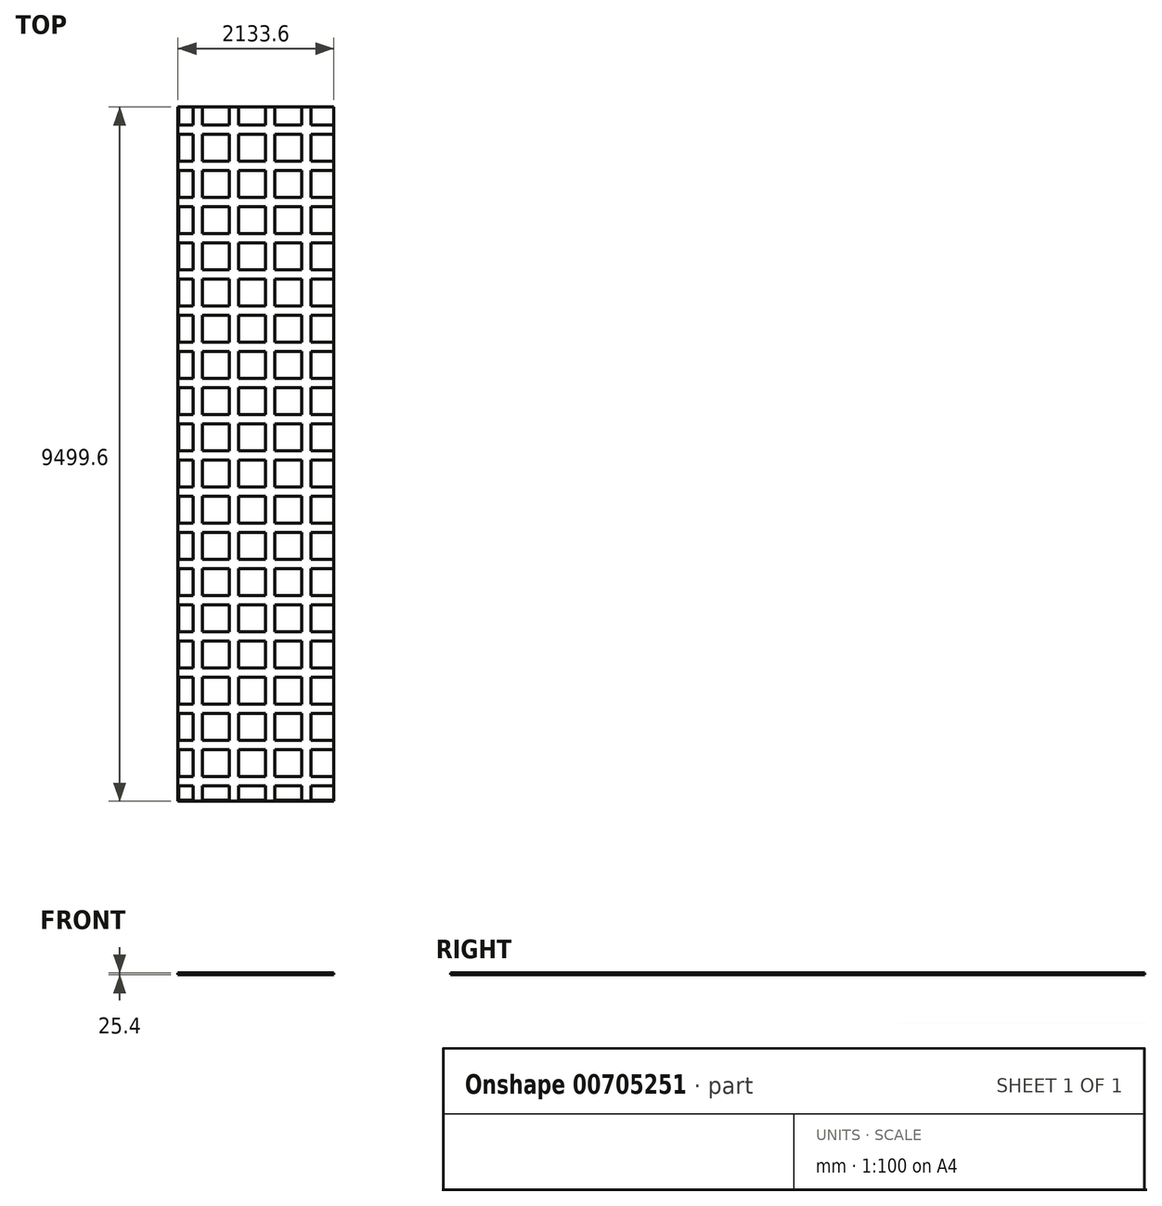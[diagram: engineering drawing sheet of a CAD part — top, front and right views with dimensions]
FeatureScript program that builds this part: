
annotation { "Feature Type Name" : "Feature", "Feature Type Description" : "" }
export const myFeature = defineFeature(function(context is Context, id is Id, definition is map)
    precondition{}
    {
        {
            var Q0;
            Q0=qCreatedBy(makeId("Top.planeOp"),FACE);
            var sketch = newSketch(context, id + "F0", { "sketchPlane" : qUnion([Q0])});
            skLineSegment(sketch, "E0.bottom", {"start": v(0, 0) * mm, "end": v(2133.6, 0) * mm});
            skLineSegment(sketch, "E0.top", {"start": v(0, 9499.6) * mm, "end": v(2133.6, 9499.6) * mm});
            skLineSegment(sketch, "E0.left", {"start": v(0, 0) * mm, "end": v(0, 9499.6) * mm});
            skLineSegment(sketch, "E0.right", {"start": v(2133.6, 0) * mm, "end": v(2133.6, 9499.6) * mm});
            skSolve(sketch);
        }
        {
            var Q0;
            Q0=makeQuery(id+"F0.imprint","IMPRINT",FACE,{"disambiguationData":[TD([[makeQuery(id+"F0.imprint","IMPRINT",EDGE,{"derivedFrom":sQuery(id+"F0.wireOp",EDGE,"E0.bottom")}),1.0]])]});
            extrude(context, id + "F1", {"entities" : qUnion([Q0]), "depth" : 25.4 * mm, "offsetDistance" : 25.4 * mm});
        }
        {
            var Q0;
            Q0=makeQuery(id+"F1.opExtrude","CAP_FACE",FACE,{"disambiguationData":[OSD([sQuery(id+"F0.wireOp",EDGE,"E0.bottom"),sQuery(id+"F0.wireOp",EDGE,"E0.top"),sQuery(id+"F0.wireOp",EDGE,"E0.left"),sQuery(id+"F0.wireOp",EDGE,"E0.right")])],"isStart":false});
            var sketch = newSketch(context, id + "F2", { "sketchPlane" : qUnion([Q0])});
            skLineSegment(sketch, "E1.0", {"start": v(12.7, 0) * mm, "end": v(12.7, 9499.6) * mm});
            skLineSegment(sketch, "E2", {"start": v(336.55, 12.7) * mm, "end": v(336.55, 9499.6) * mm});
            skLineSegment(sketch, "E3.0", {"start": v(0, 12.7) * mm, "end": v(2133.6, 12.7) * mm});
            skLineSegment(sketch, "E4", {"start": v(12.7, 336.55) * mm, "end": v(2133.6, 336.55) * mm});
            skLineSegment(sketch, "E5.0", {"start": v(209.55, 12.7) * mm, "end": v(209.55, 9499.6) * mm});
            skLineSegment(sketch, "E6.0", {"start": v(12.7, 209.55) * mm, "end": v(2133.6, 209.55) * mm});
            skLineSegment(sketch, "E7.1.0.0", {"start": v(704.85, 12.7) * mm, "end": v(704.85, 9499.6) * mm});
            skLineSegment(sketch, "E7.1.0.1", {"start": v(831.85, 12.7) * mm, "end": v(831.85, 9499.6) * mm});
            skLineSegment(sketch, "E7.2.0.0", {"start": v(1200.15, 12.7) * mm, "end": v(1200.15, 9499.6) * mm});
            skLineSegment(sketch, "E7.2.0.1", {"start": v(1327.15, 12.7) * mm, "end": v(1327.15, 9499.6) * mm});
            skLineSegment(sketch, "E7.3.0.0", {"start": v(1695.45, 12.7) * mm, "end": v(1695.45, 9499.6) * mm});
            skLineSegment(sketch, "E7.3.0.1", {"start": v(1822.45, 12.7) * mm, "end": v(1822.45, 9499.6) * mm});
            skLineSegment(sketch, "E7.direction1", {"start": v(209.55, 12.7) * mm, "end": v(704.85, 12.7) * mm, "construction": true});
            skLineSegment(sketch, "E8.0.1.0", {"start": v(12.7, 831.85) * mm, "end": v(2133.6, 831.85) * mm});
            skLineSegment(sketch, "E8.0.1.1", {"start": v(12.7, 704.85) * mm, "end": v(2133.6, 704.85) * mm});
            skLineSegment(sketch, "E8.0.2.0", {"start": v(12.7, 1327.15) * mm, "end": v(2133.6, 1327.15) * mm});
            skLineSegment(sketch, "E8.0.2.1", {"start": v(12.7, 1200.15) * mm, "end": v(2133.6, 1200.15) * mm});
            skLineSegment(sketch, "E8.0.3.0", {"start": v(12.7, 1822.45) * mm, "end": v(2133.6, 1822.45) * mm});
            skLineSegment(sketch, "E8.0.3.1", {"start": v(12.7, 1695.45) * mm, "end": v(2133.6, 1695.45) * mm});
            skLineSegment(sketch, "E8.0.4.0", {"start": v(12.7, 2317.75) * mm, "end": v(2133.6, 2317.75) * mm});
            skLineSegment(sketch, "E8.0.4.1", {"start": v(12.7, 2190.75) * mm, "end": v(2133.6, 2190.75) * mm});
            skLineSegment(sketch, "E8.0.5.0", {"start": v(12.7, 2813.05) * mm, "end": v(2133.6, 2813.05) * mm});
            skLineSegment(sketch, "E8.0.5.1", {"start": v(12.7, 2686.05) * mm, "end": v(2133.6, 2686.05) * mm});
            skLineSegment(sketch, "E8.0.6.0", {"start": v(12.7, 3308.35) * mm, "end": v(2133.6, 3308.35) * mm});
            skLineSegment(sketch, "E8.0.6.1", {"start": v(12.7, 3181.35) * mm, "end": v(2133.6, 3181.35) * mm});
            skLineSegment(sketch, "E8.0.7.0", {"start": v(12.7, 3803.65) * mm, "end": v(2133.6, 3803.65) * mm});
            skLineSegment(sketch, "E8.0.7.1", {"start": v(12.7, 3676.65) * mm, "end": v(2133.6, 3676.65) * mm});
            skLineSegment(sketch, "E8.0.8.0", {"start": v(12.7, 4298.95) * mm, "end": v(2133.6, 4298.95) * mm});
            skLineSegment(sketch, "E8.0.8.1", {"start": v(12.7, 4171.95) * mm, "end": v(2133.6, 4171.95) * mm});
            skLineSegment(sketch, "E8.0.9.0", {"start": v(12.7, 4794.25) * mm, "end": v(2133.6, 4794.25) * mm});
            skLineSegment(sketch, "E8.0.9.1", {"start": v(12.7, 4667.25) * mm, "end": v(2133.6, 4667.25) * mm});
            skLineSegment(sketch, "E8.0.10.0", {"start": v(12.7, 5289.55) * mm, "end": v(2133.6, 5289.55) * mm});
            skLineSegment(sketch, "E8.0.10.1", {"start": v(12.7, 5162.55) * mm, "end": v(2133.6, 5162.55) * mm});
            skLineSegment(sketch, "E8.0.11.0", {"start": v(12.7, 5784.85) * mm, "end": v(2133.6, 5784.85) * mm});
            skLineSegment(sketch, "E8.0.11.1", {"start": v(12.7, 5657.85) * mm, "end": v(2133.6, 5657.85) * mm});
            skLineSegment(sketch, "E8.0.12.0", {"start": v(12.7, 6280.15) * mm, "end": v(2133.6, 6280.15) * mm});
            skLineSegment(sketch, "E8.0.12.1", {"start": v(12.7, 6153.15) * mm, "end": v(2133.6, 6153.15) * mm});
            skLineSegment(sketch, "E8.0.13.0", {"start": v(12.7, 6775.45) * mm, "end": v(2133.6, 6775.45) * mm});
            skLineSegment(sketch, "E8.0.13.1", {"start": v(12.7, 6648.45) * mm, "end": v(2133.6, 6648.45) * mm});
            skLineSegment(sketch, "E8.0.14.0", {"start": v(12.7, 7270.75) * mm, "end": v(2133.6, 7270.75) * mm});
            skLineSegment(sketch, "E8.0.14.1", {"start": v(12.7, 7143.75) * mm, "end": v(2133.6, 7143.75) * mm});
            skLineSegment(sketch, "E8.0.15.0", {"start": v(12.7, 7766.05) * mm, "end": v(2133.6, 7766.05) * mm});
            skLineSegment(sketch, "E8.0.15.1", {"start": v(12.7, 7639.05) * mm, "end": v(2133.6, 7639.05) * mm});
            skLineSegment(sketch, "E8.0.16.0", {"start": v(12.7, 8261.35) * mm, "end": v(2133.6, 8261.35) * mm});
            skLineSegment(sketch, "E8.0.16.1", {"start": v(12.7, 8134.35) * mm, "end": v(2133.6, 8134.35) * mm});
            skLineSegment(sketch, "E8.0.17.0", {"start": v(12.7, 8756.65) * mm, "end": v(2133.6, 8756.65) * mm});
            skLineSegment(sketch, "E8.0.17.1", {"start": v(12.7, 8629.65) * mm, "end": v(2133.6, 8629.65) * mm});
            skLineSegment(sketch, "E8.direction1", {"start": v(12.7, 336.55) * mm, "end": v(38.1, 336.55) * mm, "construction": true});
            skLineSegment(sketch, "E8.direction2", {"start": v(12.7, 336.55) * mm, "end": v(12.7, 831.85) * mm, "construction": true});
            skLineSegment(sketch, "E9.0.0.18", {"start": v(12.7, 9251.95) * mm, "end": v(2133.6, 9251.95) * mm});
            skLineSegment(sketch, "E9.3.0.18", {"start": v(12.7, 9124.95) * mm, "end": v(2133.6, 9124.95) * mm});
            skSolve(sketch);
        }
        {
            var Q0;
            {var subQ0=sQuery(id+"F2.wireOp",EDGE,"E4");var subQ1=sQuery(id+"F2.wireOp",EDGE,"E1.0");var subQ2=makeQuery(id+"F2.imprint","INTERSECT",VERTEX,{"derivedFrom":[subQ1,subQ0]});Q0=makeQuery(id+"F2.imprint","IMPRINT",FACE,{"disambiguationData":[TD([[makeQuery(id+"F2.imprint","IMPRINT",EDGE,{"disambiguationData":[TD([[subQ2,-1.0]])],"derivedFrom":subQ1}),-1.0]])]});}
            var Q1;
            {var subQ0=sQuery(id+"F2.wireOp",EDGE,"E4");var subQ1=sQuery(id+"F2.wireOp",EDGE,"E2");var subQ2=makeQuery(id+"F2.imprint","INTERSECT",VERTEX,{"derivedFrom":[subQ1,subQ0]});Q1=makeQuery(id+"F2.imprint","IMPRINT",FACE,{"disambiguationData":[TD([[makeQuery(id+"F2.imprint","IMPRINT",EDGE,{"disambiguationData":[TD([[subQ2,-1.0]])],"derivedFrom":subQ1}),-1.0]])]});}
            var Q2;
            {var subQ0=sQuery(id+"F2.wireOp",EDGE,"E7.1.0.1");var subQ1=sQuery(id+"F2.wireOp",EDGE,"E4");var subQ2=makeQuery(id+"F2.imprint","INTERSECT",VERTEX,{"derivedFrom":[subQ1,subQ0]});Q2=makeQuery(id+"F2.imprint","IMPRINT",FACE,{"disambiguationData":[TD([[makeQuery(id+"F2.imprint","IMPRINT",EDGE,{"disambiguationData":[TD([[subQ2,-1.0]])],"derivedFrom":subQ1}),1.0]])]});}
            var Q3;
            {var subQ0=sQuery(id+"F2.wireOp",EDGE,"E7.2.0.1");var subQ1=sQuery(id+"F2.wireOp",EDGE,"E4");var subQ2=makeQuery(id+"F2.imprint","INTERSECT",VERTEX,{"derivedFrom":[subQ1,subQ0]});Q3=makeQuery(id+"F2.imprint","IMPRINT",FACE,{"disambiguationData":[TD([[makeQuery(id+"F2.imprint","IMPRINT",EDGE,{"disambiguationData":[TD([[subQ2,-1.0]])],"derivedFrom":subQ1}),1.0]])]});}
            var Q4;
            {var subQ0=sQuery(id+"F2.wireOp",EDGE,"E4");var subQ1=makeQuery(id+"F1.opExtrude","CAP_EDGE",EDGE,{"disambiguationData":[OSD([sQuery(id+"F0.wireOp",EDGE,"E0.right")])],"isStart":false});var subQ2=makeQuery(id+"F2.imprint","INTERSECT",VERTEX,{"derivedFrom":[subQ1,subQ0]});Q4=makeQuery(id+"F2.imprint","IMPRINT",FACE,{"disambiguationData":[TD([[makeQuery(id+"F2.imprint","IMPRINT",EDGE,{"disambiguationData":[TD([[subQ2,1.0]])],"derivedFrom":subQ0}),1.0]])]});}
            var Q5;
            {var subQ0=sQuery(id+"F2.wireOp",EDGE,"E8.0.1.0");var subQ1=sQuery(id+"F2.wireOp",EDGE,"E1.0");var subQ2=makeQuery(id+"F2.imprint","INTERSECT",VERTEX,{"derivedFrom":[subQ1,subQ0]});Q5=makeQuery(id+"F2.imprint","IMPRINT",FACE,{"disambiguationData":[TD([[makeQuery(id+"F2.imprint","IMPRINT",EDGE,{"disambiguationData":[TD([[subQ2,-1.0]])],"derivedFrom":subQ1}),-1.0]])]});}
            var Q6;
            {var subQ0=sQuery(id+"F2.wireOp",EDGE,"E8.0.1.0");var subQ1=sQuery(id+"F2.wireOp",EDGE,"E2");var subQ2=makeQuery(id+"F2.imprint","INTERSECT",VERTEX,{"derivedFrom":[subQ1,subQ0]});Q6=makeQuery(id+"F2.imprint","IMPRINT",FACE,{"disambiguationData":[TD([[makeQuery(id+"F2.imprint","IMPRINT",EDGE,{"disambiguationData":[TD([[subQ2,-1.0]])],"derivedFrom":subQ1}),-1.0]])]});}
            var Q7;
            {var subQ0=sQuery(id+"F2.wireOp",EDGE,"E8.0.1.0");var subQ1=sQuery(id+"F2.wireOp",EDGE,"E7.1.0.1");var subQ2=makeQuery(id+"F2.imprint","INTERSECT",VERTEX,{"derivedFrom":[subQ1,subQ0]});Q7=makeQuery(id+"F2.imprint","IMPRINT",FACE,{"disambiguationData":[TD([[makeQuery(id+"F2.imprint","IMPRINT",EDGE,{"disambiguationData":[TD([[subQ2,-1.0]])],"derivedFrom":subQ1}),-1.0]])]});}
            var Q8;
            {var subQ0=sQuery(id+"F2.wireOp",EDGE,"E8.0.1.0");var subQ1=sQuery(id+"F2.wireOp",EDGE,"E7.2.0.1");var subQ2=makeQuery(id+"F2.imprint","INTERSECT",VERTEX,{"derivedFrom":[subQ1,subQ0]});Q8=makeQuery(id+"F2.imprint","IMPRINT",FACE,{"disambiguationData":[TD([[makeQuery(id+"F2.imprint","IMPRINT",EDGE,{"disambiguationData":[TD([[subQ2,-1.0]])],"derivedFrom":subQ1}),-1.0]])]});}
            var Q9;
            {var subQ0=sQuery(id+"F2.wireOp",EDGE,"E8.0.1.0");var subQ1=sQuery(id+"F2.wireOp",EDGE,"E7.3.0.1");var subQ2=makeQuery(id+"F2.imprint","INTERSECT",VERTEX,{"derivedFrom":[subQ1,subQ0]});Q9=makeQuery(id+"F2.imprint","IMPRINT",FACE,{"disambiguationData":[TD([[makeQuery(id+"F2.imprint","IMPRINT",EDGE,{"disambiguationData":[TD([[subQ2,-1.0]])],"derivedFrom":subQ1}),-1.0]])]});}
            var Q10;
            {var subQ0=sQuery(id+"F2.wireOp",EDGE,"E8.0.2.0");var subQ1=sQuery(id+"F2.wireOp",EDGE,"E7.3.0.1");var subQ2=makeQuery(id+"F2.imprint","INTERSECT",VERTEX,{"derivedFrom":[subQ1,subQ0]});Q10=makeQuery(id+"F2.imprint","IMPRINT",FACE,{"disambiguationData":[TD([[makeQuery(id+"F2.imprint","IMPRINT",EDGE,{"disambiguationData":[TD([[subQ2,-1.0]])],"derivedFrom":subQ1}),-1.0]])]});}
            var Q11;
            {var subQ0=sQuery(id+"F2.wireOp",EDGE,"E8.0.2.0");var subQ1=sQuery(id+"F2.wireOp",EDGE,"E7.2.0.1");var subQ2=makeQuery(id+"F2.imprint","INTERSECT",VERTEX,{"derivedFrom":[subQ1,subQ0]});Q11=makeQuery(id+"F2.imprint","IMPRINT",FACE,{"disambiguationData":[TD([[makeQuery(id+"F2.imprint","IMPRINT",EDGE,{"disambiguationData":[TD([[subQ2,-1.0]])],"derivedFrom":subQ1}),-1.0]])]});}
            var Q12;
            {var subQ0=sQuery(id+"F2.wireOp",EDGE,"E8.0.2.0");var subQ1=sQuery(id+"F2.wireOp",EDGE,"E7.1.0.1");var subQ2=makeQuery(id+"F2.imprint","INTERSECT",VERTEX,{"derivedFrom":[subQ1,subQ0]});Q12=makeQuery(id+"F2.imprint","IMPRINT",FACE,{"disambiguationData":[TD([[makeQuery(id+"F2.imprint","IMPRINT",EDGE,{"disambiguationData":[TD([[subQ2,-1.0]])],"derivedFrom":subQ1}),-1.0]])]});}
            var Q13;
            {var subQ0=sQuery(id+"F2.wireOp",EDGE,"E8.0.2.0");var subQ1=sQuery(id+"F2.wireOp",EDGE,"E2");var subQ2=makeQuery(id+"F2.imprint","INTERSECT",VERTEX,{"derivedFrom":[subQ1,subQ0]});Q13=makeQuery(id+"F2.imprint","IMPRINT",FACE,{"disambiguationData":[TD([[makeQuery(id+"F2.imprint","IMPRINT",EDGE,{"disambiguationData":[TD([[subQ2,-1.0]])],"derivedFrom":subQ1}),-1.0]])]});}
            var Q14;
            {var subQ0=sQuery(id+"F2.wireOp",EDGE,"E8.0.2.0");var subQ1=sQuery(id+"F2.wireOp",EDGE,"E1.0");var subQ2=makeQuery(id+"F2.imprint","INTERSECT",VERTEX,{"derivedFrom":[subQ1,subQ0]});Q14=makeQuery(id+"F2.imprint","IMPRINT",FACE,{"disambiguationData":[TD([[makeQuery(id+"F2.imprint","IMPRINT",EDGE,{"disambiguationData":[TD([[subQ2,-1.0]])],"derivedFrom":subQ1}),-1.0]])]});}
            var Q15;
            {var subQ0=sQuery(id+"F2.wireOp",EDGE,"E8.0.3.0");var subQ1=sQuery(id+"F2.wireOp",EDGE,"E1.0");var subQ2=makeQuery(id+"F2.imprint","INTERSECT",VERTEX,{"derivedFrom":[subQ1,subQ0]});Q15=makeQuery(id+"F2.imprint","IMPRINT",FACE,{"disambiguationData":[TD([[makeQuery(id+"F2.imprint","IMPRINT",EDGE,{"disambiguationData":[TD([[subQ2,-1.0]])],"derivedFrom":subQ1}),-1.0]])]});}
            var Q16;
            {var subQ0=sQuery(id+"F2.wireOp",EDGE,"E8.0.3.0");var subQ1=sQuery(id+"F2.wireOp",EDGE,"E2");var subQ2=makeQuery(id+"F2.imprint","INTERSECT",VERTEX,{"derivedFrom":[subQ1,subQ0]});Q16=makeQuery(id+"F2.imprint","IMPRINT",FACE,{"disambiguationData":[TD([[makeQuery(id+"F2.imprint","IMPRINT",EDGE,{"disambiguationData":[TD([[subQ2,-1.0]])],"derivedFrom":subQ1}),-1.0]])]});}
            var Q17;
            {var subQ0=sQuery(id+"F2.wireOp",EDGE,"E8.0.3.0");var subQ1=sQuery(id+"F2.wireOp",EDGE,"E7.1.0.1");var subQ2=makeQuery(id+"F2.imprint","INTERSECT",VERTEX,{"derivedFrom":[subQ1,subQ0]});Q17=makeQuery(id+"F2.imprint","IMPRINT",FACE,{"disambiguationData":[TD([[makeQuery(id+"F2.imprint","IMPRINT",EDGE,{"disambiguationData":[TD([[subQ2,-1.0]])],"derivedFrom":subQ1}),-1.0]])]});}
            var Q18;
            {var subQ0=sQuery(id+"F2.wireOp",EDGE,"E8.0.3.0");var subQ1=sQuery(id+"F2.wireOp",EDGE,"E7.2.0.1");var subQ2=makeQuery(id+"F2.imprint","INTERSECT",VERTEX,{"derivedFrom":[subQ1,subQ0]});Q18=makeQuery(id+"F2.imprint","IMPRINT",FACE,{"disambiguationData":[TD([[makeQuery(id+"F2.imprint","IMPRINT",EDGE,{"disambiguationData":[TD([[subQ2,-1.0]])],"derivedFrom":subQ1}),-1.0]])]});}
            var Q19;
            {var subQ0=sQuery(id+"F2.wireOp",EDGE,"E8.0.3.0");var subQ1=sQuery(id+"F2.wireOp",EDGE,"E7.3.0.1");var subQ2=makeQuery(id+"F2.imprint","INTERSECT",VERTEX,{"derivedFrom":[subQ1,subQ0]});Q19=makeQuery(id+"F2.imprint","IMPRINT",FACE,{"disambiguationData":[TD([[makeQuery(id+"F2.imprint","IMPRINT",EDGE,{"disambiguationData":[TD([[subQ2,-1.0]])],"derivedFrom":subQ1}),-1.0]])]});}
            var Q20;
            {var subQ0=sQuery(id+"F2.wireOp",EDGE,"E8.0.4.0");var subQ1=sQuery(id+"F2.wireOp",EDGE,"E7.3.0.1");var subQ2=makeQuery(id+"F2.imprint","INTERSECT",VERTEX,{"derivedFrom":[subQ1,subQ0]});Q20=makeQuery(id+"F2.imprint","IMPRINT",FACE,{"disambiguationData":[TD([[makeQuery(id+"F2.imprint","IMPRINT",EDGE,{"disambiguationData":[TD([[subQ2,-1.0]])],"derivedFrom":subQ1}),-1.0]])]});}
            var Q21;
            {var subQ0=sQuery(id+"F2.wireOp",EDGE,"E8.0.4.0");var subQ1=sQuery(id+"F2.wireOp",EDGE,"E7.2.0.1");var subQ2=makeQuery(id+"F2.imprint","INTERSECT",VERTEX,{"derivedFrom":[subQ1,subQ0]});Q21=makeQuery(id+"F2.imprint","IMPRINT",FACE,{"disambiguationData":[TD([[makeQuery(id+"F2.imprint","IMPRINT",EDGE,{"disambiguationData":[TD([[subQ2,-1.0]])],"derivedFrom":subQ1}),-1.0]])]});}
            var Q22;
            {var subQ0=sQuery(id+"F2.wireOp",EDGE,"E8.0.4.0");var subQ1=sQuery(id+"F2.wireOp",EDGE,"E7.1.0.1");var subQ2=makeQuery(id+"F2.imprint","INTERSECT",VERTEX,{"derivedFrom":[subQ1,subQ0]});Q22=makeQuery(id+"F2.imprint","IMPRINT",FACE,{"disambiguationData":[TD([[makeQuery(id+"F2.imprint","IMPRINT",EDGE,{"disambiguationData":[TD([[subQ2,-1.0]])],"derivedFrom":subQ1}),-1.0]])]});}
            var Q23;
            {var subQ0=sQuery(id+"F2.wireOp",EDGE,"E8.0.4.0");var subQ1=sQuery(id+"F2.wireOp",EDGE,"E2");var subQ2=makeQuery(id+"F2.imprint","INTERSECT",VERTEX,{"derivedFrom":[subQ1,subQ0]});Q23=makeQuery(id+"F2.imprint","IMPRINT",FACE,{"disambiguationData":[TD([[makeQuery(id+"F2.imprint","IMPRINT",EDGE,{"disambiguationData":[TD([[subQ2,-1.0]])],"derivedFrom":subQ1}),-1.0]])]});}
            var Q24;
            {var subQ0=sQuery(id+"F2.wireOp",EDGE,"E8.0.4.0");var subQ1=sQuery(id+"F2.wireOp",EDGE,"E1.0");var subQ2=makeQuery(id+"F2.imprint","INTERSECT",VERTEX,{"derivedFrom":[subQ1,subQ0]});Q24=makeQuery(id+"F2.imprint","IMPRINT",FACE,{"disambiguationData":[TD([[makeQuery(id+"F2.imprint","IMPRINT",EDGE,{"disambiguationData":[TD([[subQ2,-1.0]])],"derivedFrom":subQ1}),-1.0]])]});}
            var Q25;
            {var subQ0=sQuery(id+"F2.wireOp",EDGE,"E8.0.5.0");var subQ1=sQuery(id+"F2.wireOp",EDGE,"E1.0");var subQ2=makeQuery(id+"F2.imprint","INTERSECT",VERTEX,{"derivedFrom":[subQ1,subQ0]});Q25=makeQuery(id+"F2.imprint","IMPRINT",FACE,{"disambiguationData":[TD([[makeQuery(id+"F2.imprint","IMPRINT",EDGE,{"disambiguationData":[TD([[subQ2,-1.0]])],"derivedFrom":subQ1}),-1.0]])]});}
            var Q26;
            {var subQ0=sQuery(id+"F2.wireOp",EDGE,"E8.0.5.0");var subQ1=sQuery(id+"F2.wireOp",EDGE,"E2");var subQ2=makeQuery(id+"F2.imprint","INTERSECT",VERTEX,{"derivedFrom":[subQ1,subQ0]});Q26=makeQuery(id+"F2.imprint","IMPRINT",FACE,{"disambiguationData":[TD([[makeQuery(id+"F2.imprint","IMPRINT",EDGE,{"disambiguationData":[TD([[subQ2,-1.0]])],"derivedFrom":subQ1}),-1.0]])]});}
            var Q27;
            {var subQ0=sQuery(id+"F2.wireOp",EDGE,"E8.0.5.0");var subQ1=sQuery(id+"F2.wireOp",EDGE,"E7.1.0.1");var subQ2=makeQuery(id+"F2.imprint","INTERSECT",VERTEX,{"derivedFrom":[subQ1,subQ0]});Q27=makeQuery(id+"F2.imprint","IMPRINT",FACE,{"disambiguationData":[TD([[makeQuery(id+"F2.imprint","IMPRINT",EDGE,{"disambiguationData":[TD([[subQ2,-1.0]])],"derivedFrom":subQ1}),-1.0]])]});}
            var Q28;
            {var subQ0=sQuery(id+"F2.wireOp",EDGE,"E8.0.5.0");var subQ1=sQuery(id+"F2.wireOp",EDGE,"E7.2.0.1");var subQ2=makeQuery(id+"F2.imprint","INTERSECT",VERTEX,{"derivedFrom":[subQ1,subQ0]});Q28=makeQuery(id+"F2.imprint","IMPRINT",FACE,{"disambiguationData":[TD([[makeQuery(id+"F2.imprint","IMPRINT",EDGE,{"disambiguationData":[TD([[subQ2,-1.0]])],"derivedFrom":subQ1}),-1.0]])]});}
            var Q29;
            {var subQ0=sQuery(id+"F2.wireOp",EDGE,"E8.0.5.0");var subQ1=sQuery(id+"F2.wireOp",EDGE,"E7.3.0.1");var subQ2=makeQuery(id+"F2.imprint","INTERSECT",VERTEX,{"derivedFrom":[subQ1,subQ0]});Q29=makeQuery(id+"F2.imprint","IMPRINT",FACE,{"disambiguationData":[TD([[makeQuery(id+"F2.imprint","IMPRINT",EDGE,{"disambiguationData":[TD([[subQ2,-1.0]])],"derivedFrom":subQ1}),-1.0]])]});}
            var Q30;
            {var subQ0=sQuery(id+"F2.wireOp",EDGE,"E8.0.6.0");var subQ1=sQuery(id+"F2.wireOp",EDGE,"E7.3.0.1");var subQ2=makeQuery(id+"F2.imprint","INTERSECT",VERTEX,{"derivedFrom":[subQ1,subQ0]});Q30=makeQuery(id+"F2.imprint","IMPRINT",FACE,{"disambiguationData":[TD([[makeQuery(id+"F2.imprint","IMPRINT",EDGE,{"disambiguationData":[TD([[subQ2,-1.0]])],"derivedFrom":subQ1}),-1.0]])]});}
            var Q31;
            {var subQ0=sQuery(id+"F2.wireOp",EDGE,"E8.0.6.0");var subQ1=sQuery(id+"F2.wireOp",EDGE,"E7.2.0.1");var subQ2=makeQuery(id+"F2.imprint","INTERSECT",VERTEX,{"derivedFrom":[subQ1,subQ0]});Q31=makeQuery(id+"F2.imprint","IMPRINT",FACE,{"disambiguationData":[TD([[makeQuery(id+"F2.imprint","IMPRINT",EDGE,{"disambiguationData":[TD([[subQ2,-1.0]])],"derivedFrom":subQ1}),-1.0]])]});}
            var Q32;
            {var subQ0=sQuery(id+"F2.wireOp",EDGE,"E8.0.6.0");var subQ1=sQuery(id+"F2.wireOp",EDGE,"E7.1.0.1");var subQ2=makeQuery(id+"F2.imprint","INTERSECT",VERTEX,{"derivedFrom":[subQ1,subQ0]});Q32=makeQuery(id+"F2.imprint","IMPRINT",FACE,{"disambiguationData":[TD([[makeQuery(id+"F2.imprint","IMPRINT",EDGE,{"disambiguationData":[TD([[subQ2,-1.0]])],"derivedFrom":subQ1}),-1.0]])]});}
            var Q33;
            {var subQ0=sQuery(id+"F2.wireOp",EDGE,"E8.0.6.0");var subQ1=sQuery(id+"F2.wireOp",EDGE,"E2");var subQ2=makeQuery(id+"F2.imprint","INTERSECT",VERTEX,{"derivedFrom":[subQ1,subQ0]});Q33=makeQuery(id+"F2.imprint","IMPRINT",FACE,{"disambiguationData":[TD([[makeQuery(id+"F2.imprint","IMPRINT",EDGE,{"disambiguationData":[TD([[subQ2,-1.0]])],"derivedFrom":subQ1}),-1.0]])]});}
            var Q34;
            {var subQ0=sQuery(id+"F2.wireOp",EDGE,"E8.0.6.0");var subQ1=sQuery(id+"F2.wireOp",EDGE,"E1.0");var subQ2=makeQuery(id+"F2.imprint","INTERSECT",VERTEX,{"derivedFrom":[subQ1,subQ0]});Q34=makeQuery(id+"F2.imprint","IMPRINT",FACE,{"disambiguationData":[TD([[makeQuery(id+"F2.imprint","IMPRINT",EDGE,{"disambiguationData":[TD([[subQ2,-1.0]])],"derivedFrom":subQ1}),-1.0]])]});}
            var Q35;
            {var subQ0=sQuery(id+"F2.wireOp",EDGE,"E8.0.7.0");var subQ1=sQuery(id+"F2.wireOp",EDGE,"E1.0");var subQ2=makeQuery(id+"F2.imprint","INTERSECT",VERTEX,{"derivedFrom":[subQ1,subQ0]});Q35=makeQuery(id+"F2.imprint","IMPRINT",FACE,{"disambiguationData":[TD([[makeQuery(id+"F2.imprint","IMPRINT",EDGE,{"disambiguationData":[TD([[subQ2,-1.0]])],"derivedFrom":subQ1}),-1.0]])]});}
            var Q36;
            {var subQ0=sQuery(id+"F2.wireOp",EDGE,"E8.0.7.0");var subQ1=sQuery(id+"F2.wireOp",EDGE,"E2");var subQ2=makeQuery(id+"F2.imprint","INTERSECT",VERTEX,{"derivedFrom":[subQ1,subQ0]});Q36=makeQuery(id+"F2.imprint","IMPRINT",FACE,{"disambiguationData":[TD([[makeQuery(id+"F2.imprint","IMPRINT",EDGE,{"disambiguationData":[TD([[subQ2,-1.0]])],"derivedFrom":subQ1}),-1.0]])]});}
            var Q37;
            {var subQ0=sQuery(id+"F2.wireOp",EDGE,"E8.0.7.0");var subQ1=sQuery(id+"F2.wireOp",EDGE,"E7.1.0.1");var subQ2=makeQuery(id+"F2.imprint","INTERSECT",VERTEX,{"derivedFrom":[subQ1,subQ0]});Q37=makeQuery(id+"F2.imprint","IMPRINT",FACE,{"disambiguationData":[TD([[makeQuery(id+"F2.imprint","IMPRINT",EDGE,{"disambiguationData":[TD([[subQ2,-1.0]])],"derivedFrom":subQ1}),-1.0]])]});}
            var Q38;
            {var subQ0=sQuery(id+"F2.wireOp",EDGE,"E8.0.7.0");var subQ1=sQuery(id+"F2.wireOp",EDGE,"E7.2.0.1");var subQ2=makeQuery(id+"F2.imprint","INTERSECT",VERTEX,{"derivedFrom":[subQ1,subQ0]});Q38=makeQuery(id+"F2.imprint","IMPRINT",FACE,{"disambiguationData":[TD([[makeQuery(id+"F2.imprint","IMPRINT",EDGE,{"disambiguationData":[TD([[subQ2,-1.0]])],"derivedFrom":subQ1}),-1.0]])]});}
            var Q39;
            {var subQ0=sQuery(id+"F2.wireOp",EDGE,"E8.0.7.0");var subQ1=sQuery(id+"F2.wireOp",EDGE,"E7.3.0.1");var subQ2=makeQuery(id+"F2.imprint","INTERSECT",VERTEX,{"derivedFrom":[subQ1,subQ0]});Q39=makeQuery(id+"F2.imprint","IMPRINT",FACE,{"disambiguationData":[TD([[makeQuery(id+"F2.imprint","IMPRINT",EDGE,{"disambiguationData":[TD([[subQ2,-1.0]])],"derivedFrom":subQ1}),-1.0]])]});}
            var Q40;
            {var subQ0=sQuery(id+"F2.wireOp",EDGE,"E8.0.8.0");var subQ1=sQuery(id+"F2.wireOp",EDGE,"E7.3.0.1");var subQ2=makeQuery(id+"F2.imprint","INTERSECT",VERTEX,{"derivedFrom":[subQ1,subQ0]});Q40=makeQuery(id+"F2.imprint","IMPRINT",FACE,{"disambiguationData":[TD([[makeQuery(id+"F2.imprint","IMPRINT",EDGE,{"disambiguationData":[TD([[subQ2,-1.0]])],"derivedFrom":subQ1}),-1.0]])]});}
            var Q41;
            {var subQ0=sQuery(id+"F2.wireOp",EDGE,"E8.0.8.0");var subQ1=sQuery(id+"F2.wireOp",EDGE,"E7.2.0.1");var subQ2=makeQuery(id+"F2.imprint","INTERSECT",VERTEX,{"derivedFrom":[subQ1,subQ0]});Q41=makeQuery(id+"F2.imprint","IMPRINT",FACE,{"disambiguationData":[TD([[makeQuery(id+"F2.imprint","IMPRINT",EDGE,{"disambiguationData":[TD([[subQ2,-1.0]])],"derivedFrom":subQ1}),-1.0]])]});}
            var Q42;
            {var subQ0=sQuery(id+"F2.wireOp",EDGE,"E8.0.8.0");var subQ1=sQuery(id+"F2.wireOp",EDGE,"E7.1.0.1");var subQ2=makeQuery(id+"F2.imprint","INTERSECT",VERTEX,{"derivedFrom":[subQ1,subQ0]});Q42=makeQuery(id+"F2.imprint","IMPRINT",FACE,{"disambiguationData":[TD([[makeQuery(id+"F2.imprint","IMPRINT",EDGE,{"disambiguationData":[TD([[subQ2,-1.0]])],"derivedFrom":subQ1}),-1.0]])]});}
            var Q43;
            {var subQ0=sQuery(id+"F2.wireOp",EDGE,"E8.0.8.0");var subQ1=sQuery(id+"F2.wireOp",EDGE,"E2");var subQ2=makeQuery(id+"F2.imprint","INTERSECT",VERTEX,{"derivedFrom":[subQ1,subQ0]});Q43=makeQuery(id+"F2.imprint","IMPRINT",FACE,{"disambiguationData":[TD([[makeQuery(id+"F2.imprint","IMPRINT",EDGE,{"disambiguationData":[TD([[subQ2,-1.0]])],"derivedFrom":subQ1}),-1.0]])]});}
            var Q44;
            {var subQ0=sQuery(id+"F2.wireOp",EDGE,"E8.0.8.0");var subQ1=sQuery(id+"F2.wireOp",EDGE,"E1.0");var subQ2=makeQuery(id+"F2.imprint","INTERSECT",VERTEX,{"derivedFrom":[subQ1,subQ0]});Q44=makeQuery(id+"F2.imprint","IMPRINT",FACE,{"disambiguationData":[TD([[makeQuery(id+"F2.imprint","IMPRINT",EDGE,{"disambiguationData":[TD([[subQ2,-1.0]])],"derivedFrom":subQ1}),-1.0]])]});}
            var Q45;
            {var subQ0=sQuery(id+"F2.wireOp",EDGE,"E8.0.9.0");var subQ1=sQuery(id+"F2.wireOp",EDGE,"E1.0");var subQ2=makeQuery(id+"F2.imprint","INTERSECT",VERTEX,{"derivedFrom":[subQ1,subQ0]});Q45=makeQuery(id+"F2.imprint","IMPRINT",FACE,{"disambiguationData":[TD([[makeQuery(id+"F2.imprint","IMPRINT",EDGE,{"disambiguationData":[TD([[subQ2,-1.0]])],"derivedFrom":subQ1}),-1.0]])]});}
            var Q46;
            {var subQ0=sQuery(id+"F2.wireOp",EDGE,"E8.0.9.0");var subQ1=sQuery(id+"F2.wireOp",EDGE,"E2");var subQ2=makeQuery(id+"F2.imprint","INTERSECT",VERTEX,{"derivedFrom":[subQ1,subQ0]});Q46=makeQuery(id+"F2.imprint","IMPRINT",FACE,{"disambiguationData":[TD([[makeQuery(id+"F2.imprint","IMPRINT",EDGE,{"disambiguationData":[TD([[subQ2,-1.0]])],"derivedFrom":subQ1}),-1.0]])]});}
            var Q47;
            {var subQ0=sQuery(id+"F2.wireOp",EDGE,"E8.0.9.0");var subQ1=sQuery(id+"F2.wireOp",EDGE,"E7.1.0.1");var subQ2=makeQuery(id+"F2.imprint","INTERSECT",VERTEX,{"derivedFrom":[subQ1,subQ0]});Q47=makeQuery(id+"F2.imprint","IMPRINT",FACE,{"disambiguationData":[TD([[makeQuery(id+"F2.imprint","IMPRINT",EDGE,{"disambiguationData":[TD([[subQ2,-1.0]])],"derivedFrom":subQ1}),-1.0]])]});}
            var Q48;
            {var subQ0=sQuery(id+"F2.wireOp",EDGE,"E8.0.9.0");var subQ1=sQuery(id+"F2.wireOp",EDGE,"E7.2.0.1");var subQ2=makeQuery(id+"F2.imprint","INTERSECT",VERTEX,{"derivedFrom":[subQ1,subQ0]});Q48=makeQuery(id+"F2.imprint","IMPRINT",FACE,{"disambiguationData":[TD([[makeQuery(id+"F2.imprint","IMPRINT",EDGE,{"disambiguationData":[TD([[subQ2,-1.0]])],"derivedFrom":subQ1}),-1.0]])]});}
            var Q49;
            {var subQ0=sQuery(id+"F2.wireOp",EDGE,"E8.0.9.0");var subQ1=sQuery(id+"F2.wireOp",EDGE,"E7.3.0.1");var subQ2=makeQuery(id+"F2.imprint","INTERSECT",VERTEX,{"derivedFrom":[subQ1,subQ0]});Q49=makeQuery(id+"F2.imprint","IMPRINT",FACE,{"disambiguationData":[TD([[makeQuery(id+"F2.imprint","IMPRINT",EDGE,{"disambiguationData":[TD([[subQ2,-1.0]])],"derivedFrom":subQ1}),-1.0]])]});}
            var Q50;
            {var subQ0=sQuery(id+"F2.wireOp",EDGE,"E8.0.10.0");var subQ1=sQuery(id+"F2.wireOp",EDGE,"E7.3.0.1");var subQ2=makeQuery(id+"F2.imprint","INTERSECT",VERTEX,{"derivedFrom":[subQ1,subQ0]});Q50=makeQuery(id+"F2.imprint","IMPRINT",FACE,{"disambiguationData":[TD([[makeQuery(id+"F2.imprint","IMPRINT",EDGE,{"disambiguationData":[TD([[subQ2,-1.0]])],"derivedFrom":subQ1}),-1.0]])]});}
            var Q51;
            {var subQ0=sQuery(id+"F2.wireOp",EDGE,"E8.0.10.0");var subQ1=sQuery(id+"F2.wireOp",EDGE,"E7.2.0.1");var subQ2=makeQuery(id+"F2.imprint","INTERSECT",VERTEX,{"derivedFrom":[subQ1,subQ0]});Q51=makeQuery(id+"F2.imprint","IMPRINT",FACE,{"disambiguationData":[TD([[makeQuery(id+"F2.imprint","IMPRINT",EDGE,{"disambiguationData":[TD([[subQ2,-1.0]])],"derivedFrom":subQ1}),-1.0]])]});}
            var Q52;
            {var subQ0=sQuery(id+"F2.wireOp",EDGE,"E8.0.10.0");var subQ1=sQuery(id+"F2.wireOp",EDGE,"E7.1.0.1");var subQ2=makeQuery(id+"F2.imprint","INTERSECT",VERTEX,{"derivedFrom":[subQ1,subQ0]});Q52=makeQuery(id+"F2.imprint","IMPRINT",FACE,{"disambiguationData":[TD([[makeQuery(id+"F2.imprint","IMPRINT",EDGE,{"disambiguationData":[TD([[subQ2,-1.0]])],"derivedFrom":subQ1}),-1.0]])]});}
            var Q53;
            {var subQ0=sQuery(id+"F2.wireOp",EDGE,"E8.0.10.0");var subQ1=sQuery(id+"F2.wireOp",EDGE,"E2");var subQ2=makeQuery(id+"F2.imprint","INTERSECT",VERTEX,{"derivedFrom":[subQ1,subQ0]});Q53=makeQuery(id+"F2.imprint","IMPRINT",FACE,{"disambiguationData":[TD([[makeQuery(id+"F2.imprint","IMPRINT",EDGE,{"disambiguationData":[TD([[subQ2,-1.0]])],"derivedFrom":subQ1}),-1.0]])]});}
            var Q54;
            {var subQ0=sQuery(id+"F2.wireOp",EDGE,"E8.0.10.0");var subQ1=sQuery(id+"F2.wireOp",EDGE,"E1.0");var subQ2=makeQuery(id+"F2.imprint","INTERSECT",VERTEX,{"derivedFrom":[subQ1,subQ0]});Q54=makeQuery(id+"F2.imprint","IMPRINT",FACE,{"disambiguationData":[TD([[makeQuery(id+"F2.imprint","IMPRINT",EDGE,{"disambiguationData":[TD([[subQ2,-1.0]])],"derivedFrom":subQ1}),-1.0]])]});}
            var Q55;
            {var subQ0=sQuery(id+"F2.wireOp",EDGE,"E8.0.11.0");var subQ1=sQuery(id+"F2.wireOp",EDGE,"E1.0");var subQ2=makeQuery(id+"F2.imprint","INTERSECT",VERTEX,{"derivedFrom":[subQ1,subQ0]});Q55=makeQuery(id+"F2.imprint","IMPRINT",FACE,{"disambiguationData":[TD([[makeQuery(id+"F2.imprint","IMPRINT",EDGE,{"disambiguationData":[TD([[subQ2,-1.0]])],"derivedFrom":subQ1}),-1.0]])]});}
            var Q56;
            {var subQ0=sQuery(id+"F2.wireOp",EDGE,"E8.0.11.0");var subQ1=sQuery(id+"F2.wireOp",EDGE,"E2");var subQ2=makeQuery(id+"F2.imprint","INTERSECT",VERTEX,{"derivedFrom":[subQ1,subQ0]});Q56=makeQuery(id+"F2.imprint","IMPRINT",FACE,{"disambiguationData":[TD([[makeQuery(id+"F2.imprint","IMPRINT",EDGE,{"disambiguationData":[TD([[subQ2,-1.0]])],"derivedFrom":subQ1}),-1.0]])]});}
            var Q57;
            {var subQ0=sQuery(id+"F2.wireOp",EDGE,"E8.0.11.0");var subQ1=sQuery(id+"F2.wireOp",EDGE,"E7.1.0.1");var subQ2=makeQuery(id+"F2.imprint","INTERSECT",VERTEX,{"derivedFrom":[subQ1,subQ0]});Q57=makeQuery(id+"F2.imprint","IMPRINT",FACE,{"disambiguationData":[TD([[makeQuery(id+"F2.imprint","IMPRINT",EDGE,{"disambiguationData":[TD([[subQ2,-1.0]])],"derivedFrom":subQ1}),-1.0]])]});}
            var Q58;
            {var subQ0=sQuery(id+"F2.wireOp",EDGE,"E8.0.11.0");var subQ1=sQuery(id+"F2.wireOp",EDGE,"E7.2.0.1");var subQ2=makeQuery(id+"F2.imprint","INTERSECT",VERTEX,{"derivedFrom":[subQ1,subQ0]});Q58=makeQuery(id+"F2.imprint","IMPRINT",FACE,{"disambiguationData":[TD([[makeQuery(id+"F2.imprint","IMPRINT",EDGE,{"disambiguationData":[TD([[subQ2,-1.0]])],"derivedFrom":subQ1}),-1.0]])]});}
            var Q59;
            {var subQ0=sQuery(id+"F2.wireOp",EDGE,"E8.0.11.0");var subQ1=sQuery(id+"F2.wireOp",EDGE,"E7.3.0.1");var subQ2=makeQuery(id+"F2.imprint","INTERSECT",VERTEX,{"derivedFrom":[subQ1,subQ0]});Q59=makeQuery(id+"F2.imprint","IMPRINT",FACE,{"disambiguationData":[TD([[makeQuery(id+"F2.imprint","IMPRINT",EDGE,{"disambiguationData":[TD([[subQ2,-1.0]])],"derivedFrom":subQ1}),-1.0]])]});}
            var Q60;
            {var subQ0=sQuery(id+"F2.wireOp",EDGE,"E8.0.12.0");var subQ1=sQuery(id+"F2.wireOp",EDGE,"E7.3.0.1");var subQ2=makeQuery(id+"F2.imprint","INTERSECT",VERTEX,{"derivedFrom":[subQ1,subQ0]});Q60=makeQuery(id+"F2.imprint","IMPRINT",FACE,{"disambiguationData":[TD([[makeQuery(id+"F2.imprint","IMPRINT",EDGE,{"disambiguationData":[TD([[subQ2,-1.0]])],"derivedFrom":subQ1}),-1.0]])]});}
            var Q61;
            {var subQ0=sQuery(id+"F2.wireOp",EDGE,"E8.0.12.0");var subQ1=sQuery(id+"F2.wireOp",EDGE,"E7.2.0.1");var subQ2=makeQuery(id+"F2.imprint","INTERSECT",VERTEX,{"derivedFrom":[subQ1,subQ0]});Q61=makeQuery(id+"F2.imprint","IMPRINT",FACE,{"disambiguationData":[TD([[makeQuery(id+"F2.imprint","IMPRINT",EDGE,{"disambiguationData":[TD([[subQ2,-1.0]])],"derivedFrom":subQ1}),-1.0]])]});}
            var Q62;
            {var subQ0=sQuery(id+"F2.wireOp",EDGE,"E8.0.12.0");var subQ1=sQuery(id+"F2.wireOp",EDGE,"E7.1.0.1");var subQ2=makeQuery(id+"F2.imprint","INTERSECT",VERTEX,{"derivedFrom":[subQ1,subQ0]});Q62=makeQuery(id+"F2.imprint","IMPRINT",FACE,{"disambiguationData":[TD([[makeQuery(id+"F2.imprint","IMPRINT",EDGE,{"disambiguationData":[TD([[subQ2,-1.0]])],"derivedFrom":subQ1}),-1.0]])]});}
            var Q63;
            {var subQ0=sQuery(id+"F2.wireOp",EDGE,"E8.0.12.0");var subQ1=sQuery(id+"F2.wireOp",EDGE,"E2");var subQ2=makeQuery(id+"F2.imprint","INTERSECT",VERTEX,{"derivedFrom":[subQ1,subQ0]});Q63=makeQuery(id+"F2.imprint","IMPRINT",FACE,{"disambiguationData":[TD([[makeQuery(id+"F2.imprint","IMPRINT",EDGE,{"disambiguationData":[TD([[subQ2,-1.0]])],"derivedFrom":subQ1}),-1.0]])]});}
            var Q64;
            {var subQ0=sQuery(id+"F2.wireOp",EDGE,"E8.0.12.0");var subQ1=sQuery(id+"F2.wireOp",EDGE,"E1.0");var subQ2=makeQuery(id+"F2.imprint","INTERSECT",VERTEX,{"derivedFrom":[subQ1,subQ0]});Q64=makeQuery(id+"F2.imprint","IMPRINT",FACE,{"disambiguationData":[TD([[makeQuery(id+"F2.imprint","IMPRINT",EDGE,{"disambiguationData":[TD([[subQ2,-1.0]])],"derivedFrom":subQ1}),-1.0]])]});}
            var Q65;
            {var subQ0=sQuery(id+"F2.wireOp",EDGE,"E8.0.13.0");var subQ1=sQuery(id+"F2.wireOp",EDGE,"E1.0");var subQ2=makeQuery(id+"F2.imprint","INTERSECT",VERTEX,{"derivedFrom":[subQ1,subQ0]});Q65=makeQuery(id+"F2.imprint","IMPRINT",FACE,{"disambiguationData":[TD([[makeQuery(id+"F2.imprint","IMPRINT",EDGE,{"disambiguationData":[TD([[subQ2,-1.0]])],"derivedFrom":subQ1}),-1.0]])]});}
            var Q66;
            {var subQ0=sQuery(id+"F2.wireOp",EDGE,"E8.0.13.0");var subQ1=sQuery(id+"F2.wireOp",EDGE,"E2");var subQ2=makeQuery(id+"F2.imprint","INTERSECT",VERTEX,{"derivedFrom":[subQ1,subQ0]});Q66=makeQuery(id+"F2.imprint","IMPRINT",FACE,{"disambiguationData":[TD([[makeQuery(id+"F2.imprint","IMPRINT",EDGE,{"disambiguationData":[TD([[subQ2,-1.0]])],"derivedFrom":subQ1}),-1.0]])]});}
            var Q67;
            {var subQ0=sQuery(id+"F2.wireOp",EDGE,"E8.0.13.0");var subQ1=sQuery(id+"F2.wireOp",EDGE,"E7.1.0.1");var subQ2=makeQuery(id+"F2.imprint","INTERSECT",VERTEX,{"derivedFrom":[subQ1,subQ0]});Q67=makeQuery(id+"F2.imprint","IMPRINT",FACE,{"disambiguationData":[TD([[makeQuery(id+"F2.imprint","IMPRINT",EDGE,{"disambiguationData":[TD([[subQ2,-1.0]])],"derivedFrom":subQ1}),-1.0]])]});}
            var Q68;
            {var subQ0=sQuery(id+"F2.wireOp",EDGE,"E8.0.13.0");var subQ1=sQuery(id+"F2.wireOp",EDGE,"E7.2.0.1");var subQ2=makeQuery(id+"F2.imprint","INTERSECT",VERTEX,{"derivedFrom":[subQ1,subQ0]});Q68=makeQuery(id+"F2.imprint","IMPRINT",FACE,{"disambiguationData":[TD([[makeQuery(id+"F2.imprint","IMPRINT",EDGE,{"disambiguationData":[TD([[subQ2,-1.0]])],"derivedFrom":subQ1}),-1.0]])]});}
            var Q69;
            {var subQ0=sQuery(id+"F2.wireOp",EDGE,"E8.0.13.0");var subQ1=sQuery(id+"F2.wireOp",EDGE,"E7.3.0.1");var subQ2=makeQuery(id+"F2.imprint","INTERSECT",VERTEX,{"derivedFrom":[subQ1,subQ0]});Q69=makeQuery(id+"F2.imprint","IMPRINT",FACE,{"disambiguationData":[TD([[makeQuery(id+"F2.imprint","IMPRINT",EDGE,{"disambiguationData":[TD([[subQ2,-1.0]])],"derivedFrom":subQ1}),-1.0]])]});}
            var Q70;
            {var subQ0=sQuery(id+"F2.wireOp",EDGE,"E8.0.14.0");var subQ1=sQuery(id+"F2.wireOp",EDGE,"E7.3.0.1");var subQ2=makeQuery(id+"F2.imprint","INTERSECT",VERTEX,{"derivedFrom":[subQ1,subQ0]});Q70=makeQuery(id+"F2.imprint","IMPRINT",FACE,{"disambiguationData":[TD([[makeQuery(id+"F2.imprint","IMPRINT",EDGE,{"disambiguationData":[TD([[subQ2,-1.0]])],"derivedFrom":subQ1}),-1.0]])]});}
            var Q71;
            {var subQ0=sQuery(id+"F2.wireOp",EDGE,"E8.0.14.0");var subQ1=sQuery(id+"F2.wireOp",EDGE,"E7.2.0.1");var subQ2=makeQuery(id+"F2.imprint","INTERSECT",VERTEX,{"derivedFrom":[subQ1,subQ0]});Q71=makeQuery(id+"F2.imprint","IMPRINT",FACE,{"disambiguationData":[TD([[makeQuery(id+"F2.imprint","IMPRINT",EDGE,{"disambiguationData":[TD([[subQ2,-1.0]])],"derivedFrom":subQ1}),-1.0]])]});}
            var Q72;
            {var subQ0=sQuery(id+"F2.wireOp",EDGE,"E8.0.14.0");var subQ1=sQuery(id+"F2.wireOp",EDGE,"E7.1.0.1");var subQ2=makeQuery(id+"F2.imprint","INTERSECT",VERTEX,{"derivedFrom":[subQ1,subQ0]});Q72=makeQuery(id+"F2.imprint","IMPRINT",FACE,{"disambiguationData":[TD([[makeQuery(id+"F2.imprint","IMPRINT",EDGE,{"disambiguationData":[TD([[subQ2,-1.0]])],"derivedFrom":subQ1}),-1.0]])]});}
            var Q73;
            {var subQ0=sQuery(id+"F2.wireOp",EDGE,"E8.0.14.0");var subQ1=sQuery(id+"F2.wireOp",EDGE,"E2");var subQ2=makeQuery(id+"F2.imprint","INTERSECT",VERTEX,{"derivedFrom":[subQ1,subQ0]});Q73=makeQuery(id+"F2.imprint","IMPRINT",FACE,{"disambiguationData":[TD([[makeQuery(id+"F2.imprint","IMPRINT",EDGE,{"disambiguationData":[TD([[subQ2,-1.0]])],"derivedFrom":subQ1}),-1.0]])]});}
            var Q74;
            {var subQ0=sQuery(id+"F2.wireOp",EDGE,"E8.0.14.0");var subQ1=sQuery(id+"F2.wireOp",EDGE,"E1.0");var subQ2=makeQuery(id+"F2.imprint","INTERSECT",VERTEX,{"derivedFrom":[subQ1,subQ0]});Q74=makeQuery(id+"F2.imprint","IMPRINT",FACE,{"disambiguationData":[TD([[makeQuery(id+"F2.imprint","IMPRINT",EDGE,{"disambiguationData":[TD([[subQ2,-1.0]])],"derivedFrom":subQ1}),-1.0]])]});}
            var Q75;
            {var subQ0=sQuery(id+"F2.wireOp",EDGE,"E8.0.15.0");var subQ1=sQuery(id+"F2.wireOp",EDGE,"E1.0");var subQ2=makeQuery(id+"F2.imprint","INTERSECT",VERTEX,{"derivedFrom":[subQ1,subQ0]});Q75=makeQuery(id+"F2.imprint","IMPRINT",FACE,{"disambiguationData":[TD([[makeQuery(id+"F2.imprint","IMPRINT",EDGE,{"disambiguationData":[TD([[subQ2,-1.0]])],"derivedFrom":subQ1}),-1.0]])]});}
            var Q76;
            {var subQ0=sQuery(id+"F2.wireOp",EDGE,"E8.0.15.0");var subQ1=sQuery(id+"F2.wireOp",EDGE,"E2");var subQ2=makeQuery(id+"F2.imprint","INTERSECT",VERTEX,{"derivedFrom":[subQ1,subQ0]});Q76=makeQuery(id+"F2.imprint","IMPRINT",FACE,{"disambiguationData":[TD([[makeQuery(id+"F2.imprint","IMPRINT",EDGE,{"disambiguationData":[TD([[subQ2,-1.0]])],"derivedFrom":subQ1}),-1.0]])]});}
            var Q77;
            {var subQ0=sQuery(id+"F2.wireOp",EDGE,"E8.0.15.0");var subQ1=sQuery(id+"F2.wireOp",EDGE,"E7.1.0.1");var subQ2=makeQuery(id+"F2.imprint","INTERSECT",VERTEX,{"derivedFrom":[subQ1,subQ0]});Q77=makeQuery(id+"F2.imprint","IMPRINT",FACE,{"disambiguationData":[TD([[makeQuery(id+"F2.imprint","IMPRINT",EDGE,{"disambiguationData":[TD([[subQ2,-1.0]])],"derivedFrom":subQ1}),-1.0]])]});}
            var Q78;
            {var subQ0=sQuery(id+"F2.wireOp",EDGE,"E8.0.15.0");var subQ1=sQuery(id+"F2.wireOp",EDGE,"E7.2.0.1");var subQ2=makeQuery(id+"F2.imprint","INTERSECT",VERTEX,{"derivedFrom":[subQ1,subQ0]});Q78=makeQuery(id+"F2.imprint","IMPRINT",FACE,{"disambiguationData":[TD([[makeQuery(id+"F2.imprint","IMPRINT",EDGE,{"disambiguationData":[TD([[subQ2,-1.0]])],"derivedFrom":subQ1}),-1.0]])]});}
            var Q79;
            {var subQ0=sQuery(id+"F2.wireOp",EDGE,"E8.0.15.0");var subQ1=sQuery(id+"F2.wireOp",EDGE,"E7.3.0.1");var subQ2=makeQuery(id+"F2.imprint","INTERSECT",VERTEX,{"derivedFrom":[subQ1,subQ0]});Q79=makeQuery(id+"F2.imprint","IMPRINT",FACE,{"disambiguationData":[TD([[makeQuery(id+"F2.imprint","IMPRINT",EDGE,{"disambiguationData":[TD([[subQ2,-1.0]])],"derivedFrom":subQ1}),-1.0]])]});}
            var Q80;
            {var subQ0=sQuery(id+"F2.wireOp",EDGE,"E8.0.16.0");var subQ1=sQuery(id+"F2.wireOp",EDGE,"E7.3.0.1");var subQ2=makeQuery(id+"F2.imprint","INTERSECT",VERTEX,{"derivedFrom":[subQ1,subQ0]});Q80=makeQuery(id+"F2.imprint","IMPRINT",FACE,{"disambiguationData":[TD([[makeQuery(id+"F2.imprint","IMPRINT",EDGE,{"disambiguationData":[TD([[subQ2,-1.0]])],"derivedFrom":subQ1}),-1.0]])]});}
            var Q81;
            {var subQ0=sQuery(id+"F2.wireOp",EDGE,"E8.0.16.0");var subQ1=sQuery(id+"F2.wireOp",EDGE,"E7.2.0.1");var subQ2=makeQuery(id+"F2.imprint","INTERSECT",VERTEX,{"derivedFrom":[subQ1,subQ0]});Q81=makeQuery(id+"F2.imprint","IMPRINT",FACE,{"disambiguationData":[TD([[makeQuery(id+"F2.imprint","IMPRINT",EDGE,{"disambiguationData":[TD([[subQ2,-1.0]])],"derivedFrom":subQ1}),-1.0]])]});}
            var Q82;
            {var subQ0=sQuery(id+"F2.wireOp",EDGE,"E8.0.16.0");var subQ1=sQuery(id+"F2.wireOp",EDGE,"E7.1.0.1");var subQ2=makeQuery(id+"F2.imprint","INTERSECT",VERTEX,{"derivedFrom":[subQ1,subQ0]});Q82=makeQuery(id+"F2.imprint","IMPRINT",FACE,{"disambiguationData":[TD([[makeQuery(id+"F2.imprint","IMPRINT",EDGE,{"disambiguationData":[TD([[subQ2,-1.0]])],"derivedFrom":subQ1}),-1.0]])]});}
            var Q83;
            {var subQ0=sQuery(id+"F2.wireOp",EDGE,"E8.0.16.0");var subQ1=sQuery(id+"F2.wireOp",EDGE,"E2");var subQ2=makeQuery(id+"F2.imprint","INTERSECT",VERTEX,{"derivedFrom":[subQ1,subQ0]});Q83=makeQuery(id+"F2.imprint","IMPRINT",FACE,{"disambiguationData":[TD([[makeQuery(id+"F2.imprint","IMPRINT",EDGE,{"disambiguationData":[TD([[subQ2,-1.0]])],"derivedFrom":subQ1}),-1.0]])]});}
            var Q84;
            {var subQ0=sQuery(id+"F2.wireOp",EDGE,"E8.0.16.0");var subQ1=sQuery(id+"F2.wireOp",EDGE,"E1.0");var subQ2=makeQuery(id+"F2.imprint","INTERSECT",VERTEX,{"derivedFrom":[subQ1,subQ0]});Q84=makeQuery(id+"F2.imprint","IMPRINT",FACE,{"disambiguationData":[TD([[makeQuery(id+"F2.imprint","IMPRINT",EDGE,{"disambiguationData":[TD([[subQ2,-1.0]])],"derivedFrom":subQ1}),-1.0]])]});}
            var Q85;
            {var subQ0=sQuery(id+"F2.wireOp",EDGE,"E8.0.17.0");var subQ1=sQuery(id+"F2.wireOp",EDGE,"E1.0");var subQ2=makeQuery(id+"F2.imprint","INTERSECT",VERTEX,{"derivedFrom":[subQ1,subQ0]});Q85=makeQuery(id+"F2.imprint","IMPRINT",FACE,{"disambiguationData":[TD([[makeQuery(id+"F2.imprint","IMPRINT",EDGE,{"disambiguationData":[TD([[subQ2,-1.0]])],"derivedFrom":subQ1}),-1.0]])]});}
            var Q86;
            {var subQ0=sQuery(id+"F2.wireOp",EDGE,"E8.0.17.0");var subQ1=sQuery(id+"F2.wireOp",EDGE,"E2");var subQ2=makeQuery(id+"F2.imprint","INTERSECT",VERTEX,{"derivedFrom":[subQ1,subQ0]});Q86=makeQuery(id+"F2.imprint","IMPRINT",FACE,{"disambiguationData":[TD([[makeQuery(id+"F2.imprint","IMPRINT",EDGE,{"disambiguationData":[TD([[subQ2,-1.0]])],"derivedFrom":subQ1}),-1.0]])]});}
            var Q87;
            {var subQ0=sQuery(id+"F2.wireOp",EDGE,"E8.0.17.0");var subQ1=sQuery(id+"F2.wireOp",EDGE,"E7.1.0.1");var subQ2=makeQuery(id+"F2.imprint","INTERSECT",VERTEX,{"derivedFrom":[subQ1,subQ0]});Q87=makeQuery(id+"F2.imprint","IMPRINT",FACE,{"disambiguationData":[TD([[makeQuery(id+"F2.imprint","IMPRINT",EDGE,{"disambiguationData":[TD([[subQ2,-1.0]])],"derivedFrom":subQ1}),-1.0]])]});}
            var Q88;
            {var subQ0=sQuery(id+"F2.wireOp",EDGE,"E8.0.17.0");var subQ1=sQuery(id+"F2.wireOp",EDGE,"E7.2.0.1");var subQ2=makeQuery(id+"F2.imprint","INTERSECT",VERTEX,{"derivedFrom":[subQ1,subQ0]});Q88=makeQuery(id+"F2.imprint","IMPRINT",FACE,{"disambiguationData":[TD([[makeQuery(id+"F2.imprint","IMPRINT",EDGE,{"disambiguationData":[TD([[subQ2,-1.0]])],"derivedFrom":subQ1}),-1.0]])]});}
            var Q89;
            {var subQ0=sQuery(id+"F2.wireOp",EDGE,"E8.0.17.0");var subQ1=sQuery(id+"F2.wireOp",EDGE,"E7.3.0.1");var subQ2=makeQuery(id+"F2.imprint","INTERSECT",VERTEX,{"derivedFrom":[subQ1,subQ0]});Q89=makeQuery(id+"F2.imprint","IMPRINT",FACE,{"disambiguationData":[TD([[makeQuery(id+"F2.imprint","IMPRINT",EDGE,{"disambiguationData":[TD([[subQ2,-1.0]])],"derivedFrom":subQ1}),-1.0]])]});}
            var Q90;
            {var subQ0=sQuery(id+"F2.wireOp",EDGE,"E7.3.0.1");var subQ1=makeQuery(id+"F1.opExtrude","CAP_EDGE",EDGE,{"disambiguationData":[OSD([sQuery(id+"F0.wireOp",EDGE,"E0.top")])],"isStart":false});var subQ2=makeQuery(id+"F2.imprint","INTERSECT",VERTEX,{"derivedFrom":[subQ1,subQ0]});Q90=makeQuery(id+"F2.imprint","IMPRINT",FACE,{"disambiguationData":[TD([[makeQuery(id+"F2.imprint","IMPRINT",EDGE,{"disambiguationData":[TD([[subQ2,1.0]])],"derivedFrom":subQ0}),-1.0]])]});}
            var Q91;
            {var subQ0=sQuery(id+"F2.wireOp",EDGE,"E7.2.0.1");var subQ1=makeQuery(id+"F1.opExtrude","CAP_EDGE",EDGE,{"disambiguationData":[OSD([sQuery(id+"F0.wireOp",EDGE,"E0.top")])],"isStart":false});var subQ2=makeQuery(id+"F2.imprint","INTERSECT",VERTEX,{"derivedFrom":[subQ1,subQ0]});Q91=makeQuery(id+"F2.imprint","IMPRINT",FACE,{"disambiguationData":[TD([[makeQuery(id+"F2.imprint","IMPRINT",EDGE,{"disambiguationData":[TD([[subQ2,1.0]])],"derivedFrom":subQ0}),-1.0]])]});}
            var Q92;
            {var subQ0=sQuery(id+"F2.wireOp",EDGE,"E7.1.0.1");var subQ1=makeQuery(id+"F1.opExtrude","CAP_EDGE",EDGE,{"disambiguationData":[OSD([sQuery(id+"F0.wireOp",EDGE,"E0.top")])],"isStart":false});var subQ2=makeQuery(id+"F2.imprint","INTERSECT",VERTEX,{"derivedFrom":[subQ1,subQ0]});Q92=makeQuery(id+"F2.imprint","IMPRINT",FACE,{"disambiguationData":[TD([[makeQuery(id+"F2.imprint","IMPRINT",EDGE,{"disambiguationData":[TD([[subQ2,1.0]])],"derivedFrom":subQ0}),-1.0]])]});}
            var Q93;
            {var subQ0=sQuery(id+"F2.wireOp",EDGE,"E2");var subQ1=makeQuery(id+"F1.opExtrude","CAP_EDGE",EDGE,{"disambiguationData":[OSD([sQuery(id+"F0.wireOp",EDGE,"E0.top")])],"isStart":false});var subQ2=makeQuery(id+"F2.imprint","INTERSECT",VERTEX,{"derivedFrom":[subQ1,subQ0]});Q93=makeQuery(id+"F2.imprint","IMPRINT",FACE,{"disambiguationData":[TD([[makeQuery(id+"F2.imprint","IMPRINT",EDGE,{"disambiguationData":[TD([[subQ2,1.0]])],"derivedFrom":subQ0}),-1.0]])]});}
            var Q94;
            {var subQ0=sQuery(id+"F2.wireOp",EDGE,"E1.0");var subQ1=makeQuery(id+"F1.opExtrude","CAP_EDGE",EDGE,{"disambiguationData":[OSD([sQuery(id+"F0.wireOp",EDGE,"E0.top")])],"isStart":false});var subQ2=makeQuery(id+"F2.imprint","INTERSECT",VERTEX,{"derivedFrom":[subQ1,subQ0]});Q94=makeQuery(id+"F2.imprint","IMPRINT",FACE,{"disambiguationData":[TD([[makeQuery(id+"F2.imprint","IMPRINT",EDGE,{"disambiguationData":[TD([[subQ2,1.0]])],"derivedFrom":subQ0}),-1.0]])]});}
            var Q95;
            {var subQ0=sQuery(id+"F2.wireOp",EDGE,"E6.0");var subQ1=sQuery(id+"F2.wireOp",EDGE,"E1.0");var subQ2=makeQuery(id+"F2.imprint","INTERSECT",VERTEX,{"derivedFrom":[subQ1,subQ0]});Q95=makeQuery(id+"F2.imprint","IMPRINT",FACE,{"disambiguationData":[TD([[makeQuery(id+"F2.imprint","IMPRINT",EDGE,{"disambiguationData":[TD([[subQ2,1.0]])],"derivedFrom":subQ1}),-1.0]])]});}
            var Q96;
            {var subQ0=sQuery(id+"F2.wireOp",EDGE,"E3.0");var subQ1=sQuery(id+"F2.wireOp",EDGE,"E2");var subQ2=makeQuery(id+"F2.imprint","INTERSECT",VERTEX,{"derivedFrom":[subQ1,subQ0]});Q96=makeQuery(id+"F2.imprint","IMPRINT",FACE,{"disambiguationData":[TD([[makeQuery(id+"F2.imprint","IMPRINT",EDGE,{"disambiguationData":[TD([[subQ2,-1.0]])],"derivedFrom":subQ1}),-1.0]])]});}
            var Q97;
            {var subQ0=sQuery(id+"F2.wireOp",EDGE,"E7.1.0.1");var subQ1=sQuery(id+"F2.wireOp",EDGE,"E3.0");var subQ2=makeQuery(id+"F2.imprint","INTERSECT",VERTEX,{"derivedFrom":[subQ1,subQ0]});Q97=makeQuery(id+"F2.imprint","IMPRINT",FACE,{"disambiguationData":[TD([[makeQuery(id+"F2.imprint","IMPRINT",EDGE,{"disambiguationData":[TD([[subQ2,-1.0]])],"derivedFrom":subQ1}),1.0]])]});}
            var Q98;
            {var subQ0=sQuery(id+"F2.wireOp",EDGE,"E7.2.0.1");var subQ1=sQuery(id+"F2.wireOp",EDGE,"E3.0");var subQ2=makeQuery(id+"F2.imprint","INTERSECT",VERTEX,{"derivedFrom":[subQ1,subQ0]});Q98=makeQuery(id+"F2.imprint","IMPRINT",FACE,{"disambiguationData":[TD([[makeQuery(id+"F2.imprint","IMPRINT",EDGE,{"disambiguationData":[TD([[subQ2,-1.0]])],"derivedFrom":subQ1}),1.0]])]});}
            var Q99;
            {var subQ0=sQuery(id+"F2.wireOp",EDGE,"E3.0");var subQ1=makeQuery(id+"F1.opExtrude","CAP_EDGE",EDGE,{"disambiguationData":[OSD([sQuery(id+"F0.wireOp",EDGE,"E0.right")])],"isStart":false});var subQ2=makeQuery(id+"F2.imprint","INTERSECT",VERTEX,{"derivedFrom":[subQ1,subQ0]});Q99=makeQuery(id+"F2.imprint","IMPRINT",FACE,{"disambiguationData":[TD([[makeQuery(id+"F2.imprint","IMPRINT",EDGE,{"disambiguationData":[TD([[subQ2,1.0]])],"derivedFrom":subQ0}),1.0]])]});}
            extrude(context, id + "F3", {"entities" : qUnion([Q0, Q1, Q2, Q3, Q4, Q5, Q6, Q7, Q8, Q9, Q10, Q11, Q12, Q13, Q14, Q15, Q16, Q17, Q18, Q19, Q20, Q21, Q22, Q23, Q24, Q25, Q26, Q27, Q28, Q29, Q30, Q31, Q32, Q33, Q34, Q35, Q36, Q37, Q38, Q39, Q40, Q41, Q42, Q43, Q44, Q45, Q46, Q47, Q48, Q49, Q50, Q51, Q52, Q53, Q54, Q55, Q56, Q57, Q58, Q59, Q60, Q61, Q62, Q63, Q64, Q65, Q66, Q67, Q68, Q69, Q70, Q71, Q72, Q73, Q74, Q75, Q76, Q77, Q78, Q79, Q80, Q81, Q82, Q83, Q84, Q85, Q86, Q87, Q88, Q89, Q90, Q91, Q92, Q93, Q94, Q95, Q96, Q97, Q98, Q99]), "operationType" : NewBodyOperationType.ADD, "depth" : 0 * mm, "offsetDistance" : 25.4 * mm});
        }
    });
